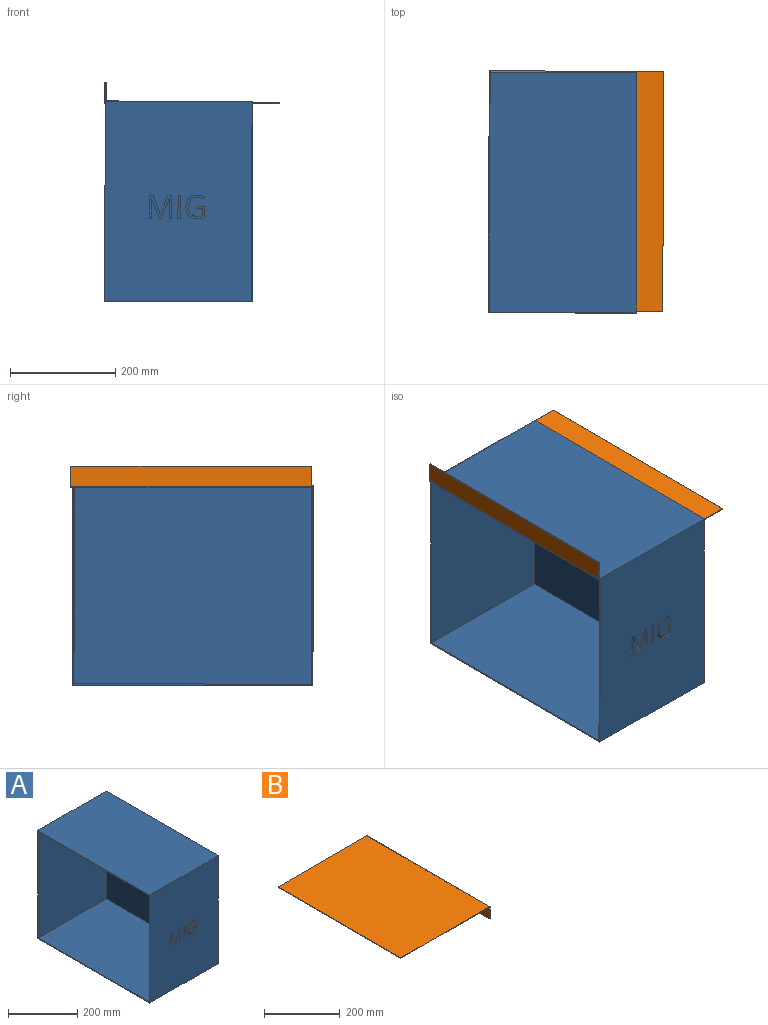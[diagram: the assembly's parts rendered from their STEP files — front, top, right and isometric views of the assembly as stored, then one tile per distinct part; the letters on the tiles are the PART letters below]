
ASSEMBLY  parts=2 mates=1
PART A: 53 faces, bbox 279.4x457.2x381 mm
  f0: plane 381x279.4mm, normal (0,-1,0), area 104850.1mm2, adj f2,f3,f4,f5,f11,f12,f13,f14
  f1: plane 375.92x276.86mm, normal (0,1,0), area 102475.9mm2, adj f2,f7,f8,f9,f11,f12,f13,f14
  f2: plane 457.2x381mm, normal (-1,0,0), area 4232.2mm2, adj f0,f1,f3,f5,f6,f7,f9,f10
  f3: plane 457.2x279.4mm, normal (0,0,-1), area 127741.7mm2, adj f0,f2,f4,f6
  f4: plane 457.2x381mm, normal (1,0,0), area 174193.2mm2, adj f0,f3,f5,f6
  f5: plane 457.2x279.4mm, normal (0,0,1), area 127741.7mm2, adj f0,f2,f4,f6
  f6: plane 381x279.4mm, normal (0,1,0), area 106451.4mm2, adj f2,f3,f4,f5
  f7: plane 452.12x276.86mm, normal (0,0,1), area 125173.9mm2, adj f1,f2,f8,f10
  f8: plane 452.12x375.92mm, normal (-1,0,0), area 169961mm2, adj f1,f7,f9,f10
  f9: plane 452.12x276.86mm, normal (0,0,-1), area 125173.9mm2, adj f1,f2,f8,f10
  f10: plane 375.92x276.86mm, normal (0,-1,0), area 104077.2mm2, adj f2,f7,f8,f9
  f11: plane 5.05x2.54mm, normal (0,0,1), area 12.8mm2, adj f0,f1,f12,f13
  f12: plane 43.49x2.54mm, normal (1,0,0), area 110.5mm2, adj f0,f1,f11,f14
  f13: plane 43.49x2.54mm, normal (-1,0,0), area 110.5mm2, adj f0,f1,f11,f14
  f14: plane 5.05x2.54mm, normal (0,0,-1), area 12.8mm2, adj f0,f1,f12,f13
  f15: plane 4.52x2.54mm, normal (1,0,0), area 11.5mm2, adj f0,f1,f16,f32
  f16: plane 9.72x2.54mm, normal (0,0,1), area 24.7mm2, adj f0,f1,f15,f17
  f17: plane 13.38x2.54mm, normal (1,0,0), area 34mm2, adj f0,f1,f16,f18
  f18: extruded ~8.83x2.54mm, area 22.6mm2, adj f0,f1,f17,f19
  f19: extruded ~12.63x4.55mm, area 35.1mm2, adj f0,f1,f18,f20
  f20: extruded ~13.36x4.3mm, area 36.5mm2, adj f0,f1,f19,f21
  f21: extruded ~13.12x4.46mm, area 36.1mm2, adj f0,f1,f20,f22
  f22: extruded ~12.4x4.73mm, area 34.7mm2, adj f0,f1,f21,f23
  f23: extruded ~11.34x2.54mm, area 29.7mm2, adj f0,f1,f22,f24
  f24: plane 4.46x2.54mm, normal (-0.92,0,0.4), area 12.4mm2, adj f0,f1,f23,f25
  f25: extruded ~12.97x2.55mm, area 33.8mm2, adj f0,f1,f24,f26
  f26: extruded ~11.98x2.69mm, area 31.5mm2, adj f0,f1,f25,f27
  f27: extruded ~7.84x7.79mm, area 28.5mm2, adj f0,f1,f26,f28
  f28: extruded ~11.89x2.72mm, area 31.3mm2, adj f0,f1,f27,f29
  f29: extruded ~16.46x5.5mm, area 45.2mm2, adj f0,f1,f28,f30
  f30: extruded ~15.37x5.88mm, area 43.1mm2, adj f0,f1,f29,f31
  f31: extruded ~8.27x2.54mm, area 21.1mm2, adj f0,f1,f30,f33
  f32: plane 14.78x2.54mm, normal (0,0,-1), area 37.5mm2, adj f0,f1,f15,f34
  f33: extruded ~7.03x2.54mm, area 18.4mm2, adj f0,f1,f31,f34
  f34: plane 21.15x2.54mm, normal (-1,0,0), area 53.7mm2, adj f0,f1,f32,f33
  f35: plane 4.07x2.54mm, normal (0,0,1), area 10.3mm2, adj f0,f1,f36,f50
  f36: plane 38.49x14.88mm, normal (-0.93,0,0.36), area 104.8mm2, adj f0,f1,f35,f37
  f37: plane 2.54x0.24mm, normal (0,0,1), area 0.6mm2, adj f0,f1,f36,f38
  f38: extruded ~10.47x2.54mm, area 26.6mm2, adj f0,f1,f37,f39
  f39: plane 28.02x2.54mm, normal (1,0,0), area 71.2mm2, adj f0,f1,f38,f40
  f40: plane 5.05x2.54mm, normal (0,0,1), area 12.8mm2, adj f0,f1,f39,f41
  f41: plane 43.49x2.54mm, normal (-1,0,0), area 110.5mm2, adj f0,f1,f40,f42
  f42: plane 7.56x2.54mm, normal (0,0,-1), area 19.2mm2, adj f0,f1,f41,f43
  f43: plane 35.88x13.89mm, normal (0.93,0,-0.36), area 97.7mm2, adj f0,f1,f42,f44
  f44: plane 2.54x0.24mm, normal (0,0,-1), area 0.6mm2, adj f0,f1,f43,f45
  f45: plane 35.88x13.77mm, normal (-0.93,0,-0.36), area 97.6mm2, adj f0,f1,f44,f46
  f46: plane 7.62x2.54mm, normal (0,0,-1), area 19.3mm2, adj f0,f1,f45,f47
  f47: plane 43.49x2.54mm, normal (1,0,0), area 110.5mm2, adj f0,f1,f46,f48
  f48: plane 4.67x2.54mm, normal (0,0,1), area 11.9mm2, adj f0,f1,f47,f49
  f49: plane 27.66x2.54mm, normal (-1,0,0), area 70.3mm2, adj f0,f1,f48,f51
  f50: plane 38.55x14.75mm, normal (0.93,0,0.36), area 104.8mm2, adj f0,f1,f35,f52
  f51: extruded ~10.89x2.54mm, area 27.7mm2, adj f0,f1,f49,f52
  f52: plane 2.54x0.24mm, normal (0,0,1), area 0.6mm2, adj f0,f1,f50,f51
PART B: 10 faces, bbox 331.8x457.2x39.7 mm
  f0: plane 457.2x328.61mm, normal (0,0,-1), area 150241.6mm2, adj f1,f7,f8,f9
  f1: cylinder r=1.59mm len=457.2mm, axis (0,1,0), area 1140.1mm2, adj f0,f2,f8,f9
  f2: plane 457.2x36.51mm, normal (-1,0,0), area 16693.5mm2, adj f1,f3,f8,f9
  f3: plane 457.2x1.59mm, normal (0,0,-1), area 725.8mm2, adj f2,f4,f8,f9
  f4: plane 457.2x38.1mm, normal (1,0,0), area 17419.3mm2, adj f3,f5,f8,f9
  f5: cylinder r=1.59mm len=457.2mm, axis (0,1,0), area 1140.1mm2, adj f4,f6,f8,f9
  f6: plane 457.2x330.2mm, normal (0,0,1), area 150967.4mm2, adj f5,f7,f8,f9
  f7: plane 457.2x1.59mm, normal (-1,0,0), area 725.8mm2, adj f0,f6,f8,f9
  f8: plane 331.79x39.69mm, normal (0,-1,0), area 588.6mm2, adj f0,f1,f2,f3,f4,f5,f6,f7
  f9: plane 331.79x39.69mm, normal (0,1,0), area 588.6mm2, adj f0,f1,f2,f3,f4,f5,f6,f7
PLACE A rot(axis=(0.15,0.5,-0.85),0.2deg) t=(-445.2,32.53,-77.8)mm fixed
PLACE B rot(axis=(0,-1,0),179.9deg) t=(-584.48,35.47,110.47)mm
MATE revolute B.f1 <-> A.f1  axis (0,-1,0) through (-585.34,-193.13,110.32)mm
